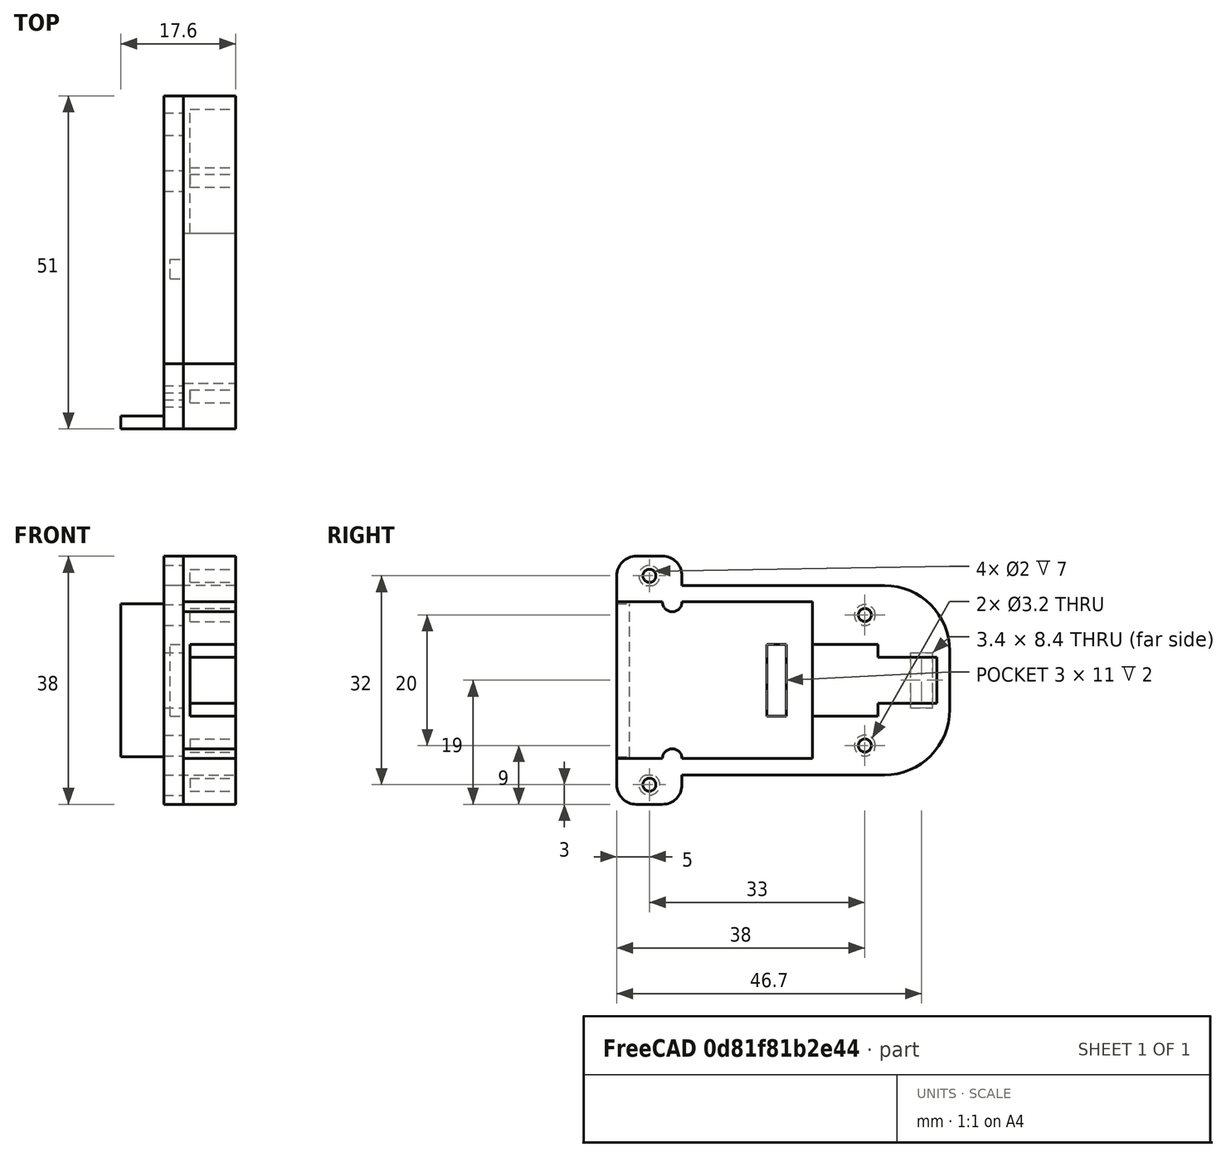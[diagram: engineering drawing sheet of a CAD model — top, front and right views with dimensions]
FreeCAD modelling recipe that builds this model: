
FCSTD DOCUMENT  (FreeCAD 0.19R)
Label: soil_sensor
License: All rights reserved
LicenseURL: http://en.wikipedia.org/wiki/All_rights_reserved
objects: Part::Box×10, Part::Cylinder×5, Part::Mirroring×5, Part::MultiFuse×4, Part::Fillet×4, Part::Cut×4, App::Part×2, Part::Feature×1, Part::Refine×1
note: 34 computed .brp shape members not serialized (recipe doc carries the construction recipe); baked Part::Feature solids carry a one-line shape summary decoded from their .brp

FEATURE [Part::Feature] Case001
  shape: bbox 11 x 50.5 x 28.2 mm, 500 faces, 0 solids (baked)
FEATURE [Part::Refine] Case001001
  Placement = pos=(-4.47802,-20.2867,11.6) rot=(0,0,1;0rad)
  Source = -> Case001
FEATURE [Part::Box] Box  label="extract cube"
  AttacherType = Attacher::AttachEngine3D
  Height = 24
  Length = 14
  Placement = pos=(-1,-23,-12) rot=(0,0,1;0rad)
  Width = 30
  expr: .Placement.Base.x = <<external cube>>.Placement.Base.x + 3mm
  expr: .Placement.Base.z = -Height / 2
FEATURE [Part::Box] Box001  label="external cube"
  AttacherType = Attacher::AttachEngine3D
  Height = 29
  Length = 11
  Placement = pos=(-4,-23,-14.5) rot=(0,0,1;0rad)
  Width = 51
  expr: .Placement.Base.z = -Height / 2
FEATURE [Part::Box] Box002  label="connector extract cube"
  AttacherType = Attacher::AttachEngine3D
  Height = 11
  Length = 11
  Placement = pos=(0,7,-5.5) rot=(0,0,1;0rad)
  Width = 10
  expr: .Placement.Base.x = <<extract cube>>.Placement.Base.x + 1mm
  expr: .Placement.Base.z = -Height / 2
FEATURE [Part::Box] Box003  label="pins extraction cube"
  AttacherType = Attacher::AttachEngine3D
  Height = 11
  Length = 11
  Placement = pos=(-3,0,-5.5) rot=(0,0,1;0rad)
  Width = 3
  expr: .Placement.Base.x = <<external cube>>.Placement.Base.x + 1mm
  expr: .Placement.Base.z = -Height / 2
FEATURE [Part::Box] Box004  label="wire extract cube"
  AttacherType = Attacher::AttachEngine3D
  Height = 7
  Length = 11
  Placement = pos=(0,17,-3.5) rot=(0,0,1;0rad)
  Width = 9
  expr: .Placement.Base.x = <<extract cube>>.Placement.Base.x + 1mm
  expr: .Placement.Base.z = -Height / 2
FEATURE [Part::Cylinder] Cylinder  label="side cylinder"
  Angle = 360
  AttacherType = Attacher::AttachEngine3D
  Height = 8
  Placement = pos=(-1,-14.5,12) rot=(0,1,0;1.5708rad)
  Radius = 1.5
  expr: .Placement.Base.x = <<extract cube>>.Placement.Base.x
FEATURE [Part::Mirroring] Part__Mirroring  label="Cylinder (Mirror #1)"
  Base = (0,0,0)
  Normal = (0,0,1)
  Source = -> Cylinder
FEATURE [Part::Cylinder] Cylinder001  label="screw hole cylinder"
  Angle = 360
  AttacherType = Attacher::AttachEngine3D
  Height = 7
  Placement = pos=(0,15,10) rot=(0,1,0;1.5708rad)
  Radius = 1
FEATURE [Part::Mirroring] Part__Mirroring001  label="screw hole cylinder (Mirror #2)"
  Base = (0,0,0)
  Normal = (0,0,1)
  Source = -> Cylinder001
FEATURE [Part::MultiFuse] Fusion  label="extract fusion"
  Shapes = -> [Box002,Box,Box003,Box004,Part__Mirroring001,Cylinder001]
FEATURE [Part::Fillet] Fillet  label="external fillet"
  Base = -> Box001
  Edges = 2 edges r=10: [Edge11,Edge12]
FEATURE [Part::Cut] Cut
  Base = -> Fillet
  Tool = -> Fusion
FEATURE [Part::Box] Box005  label="side hole cube"
  AttacherType = Attacher::AttachEngine3D
  Height = 6
  Length = 11
  Placement = pos=(-4,-23,13) rot=(0,0,1;0rad)
  Width = 10
  expr: .Placement.Base.x = <<external cube>>.Placement.Base.x
  expr: Length = <<external cube>>.Length
FEATURE [Part::Fillet] Fillet001  label="side hole fillet"
  Base = -> Box005
  Edges = 2 edges r=3: [Edge10,Edge12]
FEATURE [Part::Cylinder] Cylinder002  label="screw hole cylinder001"
  Angle = 360
  AttacherType = Attacher::AttachEngine3D
  Height = 7
  Placement = pos=(-2e-15,-18,16) rot=(0,1,0;1.5708rad)
  Radius = 1
FEATURE [Part::Cut] Cut001
  Base = -> Fillet001
  Tool = -> Cylinder002
FEATURE [Part::Mirroring] Part__Mirroring002  label="Cut001 (Mirror #3)"
  Base = (0,0,0)
  Normal = (0,0,1)
  Source = -> Cut001
FEATURE [Part::MultiFuse] Fusion001  label="body fusion"
  Shapes = -> [Cut,Part__Mirroring,Cylinder,Part__Mirroring002,Cut001]
FEATURE [Part::Box] Box006  label="external cube001"
  AttacherType = Attacher::AttachEngine3D
  Height = 29
  Length = 3
  Placement = pos=(-4,-23,-14.5) rot=(0,0,1;0rad)
  Width = 51
  expr: .Placement.Base.z = -Height / 2
FEATURE [Part::Fillet] Fillet002  label="external fillet001"
  Base = -> Box006
  Edges = 2 edges r=10: [Edge11,Edge12]
FEATURE [App::Part] Part001  label="body part"
  Group = -> [Fusion001]
  Origin = -> Origin001
FEATURE [Part::Cylinder] Cylinder003  label="screw hole cylinder002"
  Angle = 360
  AttacherType = Attacher::AttachEngine3D
  Height = 7
  Placement = pos=(-7,-18,16) rot=(0,1,0;1.5708rad)
  Radius = 1.6
FEATURE [Part::Box] Box007  label="side hole cube001"
  AttacherType = Attacher::AttachEngine3D
  Height = 6
  Length = 3
  Placement = pos=(-4,-23,13) rot=(0,0,1;0rad)
  Width = 10
  expr: Length = <<external cube001>>.Length
  expr: .Placement.Base.x = <<external cube>>.Placement.Base.x
FEATURE [Part::Fillet] Fillet003  label="side hole fillet001"
  Base = -> Box007
  Edges = 2 edges r=3: [Edge10,Edge12]
FEATURE [Part::Cut] Cut002
  Base = -> Fillet003
  Tool = -> Cylinder003
FEATURE [Part::Mirroring] Part__Mirroring003  label="Cut001 (Mirror #3)001"
  Base = (0,0,0)
  Normal = (0,0,1)
  Source = -> Cut002
FEATURE [Part::Cylinder] Cylinder004  label="screw hole cylinder003"
  Angle = 360
  AttacherType = Attacher::AttachEngine3D
  Height = 7
  Placement = pos=(-6,15,10) rot=(0,1,0;1.5708rad)
  Radius = 1.6
FEATURE [Part::Mirroring] Part__Mirroring004  label="screw hole cylinder (Mirror #2)001"
  Base = (0,0,0)
  Normal = (0,0,1)
  Source = -> Cylinder004
FEATURE [Part::Box] Box008  label="wire extract cube001"
  AttacherType = Attacher::AttachEngine3D
  Height = 8.4
  Length = 11
  Placement = pos=(-4,22,-4.2) rot=(0,0,1;0rad)
  Width = 3.4
  expr: .Placement.Base.z = -Height / 2
  expr: .Placement.Base.x = <<external cube001>>.Placement.Base.x
FEATURE [Part::MultiFuse] Fusion002  label="cover extract fusion"
  Shapes = -> [Part__Mirroring004,Cylinder004,Box008]
FEATURE [Part::Box] Box009  label="external cube border"
  AttacherType = Attacher::AttachEngine3D
  Height = 23.4
  Length = 9
  Placement = pos=(-10.6,-23,-11.7) rot=(0,0,1;0rad)
  Width = 2
  expr: .Placement.Base.z = -Height / 2
FEATURE [Part::MultiFuse] Fusion003  label="cover body fusion"
  Shapes = -> [Fillet002,Part__Mirroring003,Cut002,Box009]
FEATURE [Part::Cut] Cut003  label="cover cut"
  Base = -> Fusion003
  Tool = -> Fusion002
FEATURE [App::Part] Part  label="cover part"
  Group = -> [Cut003]
  Origin = -> Origin
  Placement = pos=(11,0,0) rot=(0,0,1;0rad)
